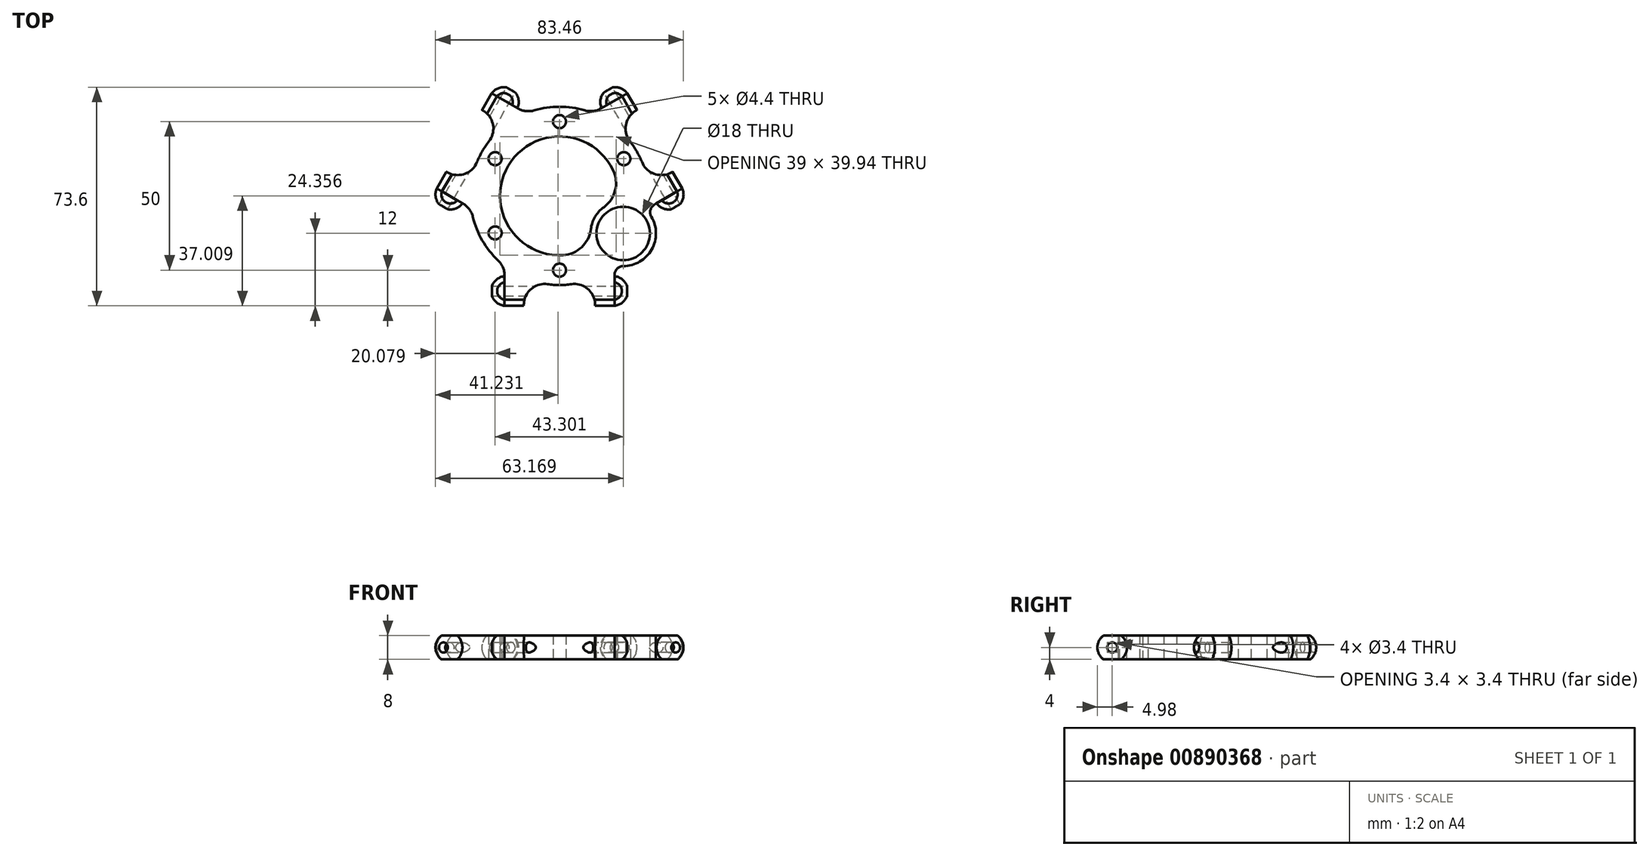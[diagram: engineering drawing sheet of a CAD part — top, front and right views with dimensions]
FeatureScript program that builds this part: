
annotation { "Feature Type Name" : "Feature", "Feature Type Description" : "" }
export const myFeature = defineFeature(function(context is Context, id is Id, definition is map)
    precondition{}
    {
        {
            var Q0;
            Q0=qCreatedBy(makeId("Top.planeOp"),FACE);
            var sketch = newSketch(context, id + "F0", { "sketchPlane" : qUnion([Q0])});
            skLineSegment(sketch, "E0", {"start": v(-16.34, 35.93) * mm, "end": v(-39.06, -3.47) * mm, "construction": true});
            skLineSegment(sketch, "E1", {"start": v(-40.4, -2.74) * mm, "end": v(-37.72, -4.2) * mm, "construction": true});
            skLineSegment(sketch, "E2", {"start": v(-17.63, 36.7) * mm, "end": v(-15.06, 35.15) * mm, "construction": true});
            skCircle(sketch, "E3", {"center": v(0, 0) * mm, "radius": 30 * mm});
            skCircle(sketch, "E4", {"center": v(0, 0) * mm, "radius": 20 * mm});
            skLineSegment(sketch, "E5", {"start": v(0, 0) * mm, "end": v(0, -43.55) * mm, "construction": true});
            skLineSegment(sketch, "E6", {"start": v(-25.45, -32) * mm, "end": v(35.74, -32) * mm, "construction": true});
            skLineSegment(sketch, "E7", {"start": v(-12, -37) * mm, "end": v(-12, -27.5) * mm});
            skLineSegment(sketch, "E8", {"start": v(-12, -37) * mm, "end": v(-18.5, -37) * mm});
            skLineSegment(sketch, "E9", {"start": v(-18.5, -37) * mm, "end": v(-18.5, -23.62) * mm});
            skLineSegment(sketch, "E10.MirrorCS", {"start": v(18.5, -37) * mm, "end": v(18.5, -23.62) * mm});
            skLineSegment(sketch, "E11.MirrorCS", {"start": v(12, -37) * mm, "end": v(12, -27.5) * mm});
            skLineSegment(sketch, "E12.MirrorCS", {"start": v(12, -37) * mm, "end": v(18.5, -37) * mm});
            skLineSegment(sketch, "E13.1.0", {"start": v(41.29, 2.48) * mm, "end": v(29.7, -4.21) * mm});
            skLineSegment(sketch, "E13.1.1", {"start": v(38.04, 8.1) * mm, "end": v(41.29, 2.48) * mm});
            skLineSegment(sketch, "E13.1.2", {"start": v(38.04, 8.1) * mm, "end": v(29.81, 3.36) * mm});
            skLineSegment(sketch, "E13.1.3", {"start": v(26.04, 28.9) * mm, "end": v(17.81, 24.14) * mm});
            skLineSegment(sketch, "E13.1.4", {"start": v(26.04, 28.9) * mm, "end": v(22.79, 34.52) * mm});
            skLineSegment(sketch, "E13.1.5", {"start": v(22.79, 34.52) * mm, "end": v(11.2, 27.83) * mm});
            skLineSegment(sketch, "E13.2.0", {"start": v(-22.79, 34.52) * mm, "end": v(-11.2, 27.83) * mm});
            skLineSegment(sketch, "E13.2.1", {"start": v(-26.04, 28.9) * mm, "end": v(-22.79, 34.52) * mm});
            skLineSegment(sketch, "E13.2.2", {"start": v(-26.04, 28.9) * mm, "end": v(-17.81, 24.14) * mm});
            skLineSegment(sketch, "E13.2.3", {"start": v(-38.04, 8.1) * mm, "end": v(-29.81, 3.36) * mm});
            skLineSegment(sketch, "E13.2.4", {"start": v(-38.04, 8.1) * mm, "end": v(-41.29, 2.48) * mm});
            skLineSegment(sketch, "E13.2.5", {"start": v(-41.29, 2.48) * mm, "end": v(-29.7, -4.21) * mm});
            skCircle(sketch, "E14", {"center": v(0, 25) * mm, "radius": 2.2 * mm});
            skCircle(sketch, "E15.1.0", {"center": v(-21.65, 12.5) * mm, "radius": 2.2 * mm});
            skCircle(sketch, "E15.2.0", {"center": v(-21.65, -12.5) * mm, "radius": 2.2 * mm});
            skCircle(sketch, "E15.3.0", {"center": v(0, -25) * mm, "radius": 2.2 * mm});
            skCircle(sketch, "E15.4.0", {"center": v(21.65, -12.5) * mm, "radius": 2.2 * mm});
            skCircle(sketch, "E15.5.0", {"center": v(21.65, 12.5) * mm, "radius": 2.2 * mm});
            skSolve(sketch);
        }
        {
            var Q0;
            Q0=qSketchRegion(id+"F0",true);
            extrude(context, id + "F1", {"entities" : qUnion([Q0]), "endBound" : BoundingType.SYMMETRIC, "depth" : 10 * mm, "offsetDistance" : 25 * mm});
        }
        {
            var Q0;
            Q0=qCreatedBy(makeId("Top.planeOp"),FACE);
            var sketch = newSketch(context, id + "F2", { "sketchPlane" : qUnion([Q0])});
            skArc(sketch, "E16", {"start": v(-23, -32.02) * mm, "mid": v(-21.7, -35.37) * mm, "end": v(-18.5, -37) * mm});
            skLineSegment(sketch, "E17", {"start": v(-18, -32.02) * mm, "end": v(-25.15, -32.02) * mm, "construction": true});
            skLineSegment(sketch, "E18", {"start": v(0, 0) * mm, "end": v(0, -44.37) * mm, "construction": true});
            skLineSegment(sketch, "E19", {"start": v(-39.92, 23.05) * mm, "end": v(0, 0) * mm, "construction": true});
            skLineSegment(sketch, "E20", {"start": v(0, 0) * mm, "end": v(41.5, 23.96) * mm, "construction": true});
            skLineSegment(sketch, "E21", {"start": v(-18.5, -37) * mm, "end": v(-18.5, -27.05) * mm});
            skLineSegment(sketch, "E22", {"start": v(-23, -32.02) * mm, "end": v(-18.5, -32.02) * mm});
            skArc(sketch, "E23.1.0", {"start": v(39.23, -3.9) * mm, "mid": v(41.49, -1.11) * mm, "end": v(41.29, 2.48) * mm});
            skLineSegment(sketch, "E23.1.1", {"start": v(39.23, -3.9) * mm, "end": v(36.98, -0.01) * mm});
            skArc(sketch, "E23.2.0", {"start": v(-16.23, 35.93) * mm, "mid": v(-19.78, 36.49) * mm, "end": v(-22.79, 34.52) * mm});
            skLineSegment(sketch, "E23.2.1", {"start": v(-16.23, 35.93) * mm, "end": v(-18.48, 32.03) * mm});
            skPoint(sketch, "E23.center", {"position": v(0, 0) * mm});
            skLineSegment(sketch, "E24.MirrorCS", {"start": v(23, -32.02) * mm, "end": v(18.5, -32.02) * mm});
            skLineSegment(sketch, "E25.MirrorCS", {"start": v(18, -32.02) * mm, "end": v(25.15, -32.02) * mm, "construction": true});
            skLineSegment(sketch, "E26.MirrorCS", {"start": v(18.5, -37) * mm, "end": v(18.5, -27.05) * mm});
            skArc(sketch, "E27.MirrorCS", {"start": v(23, -32.02) * mm, "mid": v(21.7, -35.37) * mm, "end": v(18.5, -37) * mm});
            skLineSegment(sketch, "E28", {"start": v(0, 0) * mm, "end": v(31.6, -18.24) * mm, "construction": true});
            skSolve(sketch);
        }
        {
            var Q0;
            Q0=qSketchRegion(id+"F2",true);
            var Q1;
            Q1=sQuery(id+"F2.wireOp",EDGE,"E17");
            revolve(context, id + "F3", {"surfaceOperationType" : NewSurfaceOperationType.NEW, "entities" : qUnion([Q0]), "axis" : qUnion([Q1]), "revolveType" : RevolveType.FULL});
        }
        {
            var Q0;
            Q0=qCreatedBy(makeId("Right.planeOp"),FACE);
            var sketch = newSketch(context, id + "F4", { "sketchPlane" : qUnion([Q0])});
            skLineSegment(sketch, "E29", {"start": v(0, 32.68) * mm, "end": v(0, -16.38) * mm, "construction": true});
            skSolve(sketch);
        }
        {
            var Q0;
            Q0=makeQuery(id+"F3.opRevolve","SWEPT_BODY",BODY,{"disambiguationData":[OSD([sQuery(id+"F2.wireOp",EDGE,"E16"),sQuery(id+"F2.wireOp",EDGE,"E21"),sQuery(id+"F2.wireOp",EDGE,"E22")])]});
            var Q1;
            Q1=makeQuery(id+"F3.opRevolve","SWEPT_BODY",BODY,{"disambiguationData":[OSD([sQuery(id+"F2.wireOp",EDGE,"E24.MirrorCS"),sQuery(id+"F2.wireOp",EDGE,"E26.MirrorCS"),sQuery(id+"F2.wireOp",EDGE,"E27.MirrorCS")])]});
            var Q2;
            Q2=sQuery(id+"F4.wireOp",EDGE,"E29");
            circularPattern(context, id + "F5", {"entities" : qUnion([Q0, Q1]), "axis" : qUnion([Q2]), "angle" : 360 * degree, "instanceCount" : 3, "equalSpace" : true});
        }
        {
            var Q0;
            Q0=makeQuery(id+"F1.opExtrude","CAP_EDGE",EDGE,{"disambiguationData":[OSD([sQuery(id+"F0.wireOp",EDGE,"E13.2.1")])],"isStart":false});
            var Q1;
            Q1=makeQuery(id+"F1.opExtrude","CAP_EDGE",EDGE,{"disambiguationData":[OSD([sQuery(id+"F0.wireOp",EDGE,"E13.2.4")])],"isStart":false});
            var Q2;
            Q2=makeQuery(id+"F1.opExtrude","CAP_EDGE",EDGE,{"disambiguationData":[OSD([sQuery(id+"F0.wireOp",EDGE,"E13.1.4")])],"isStart":false});
            var Q3;
            Q3=makeQuery(id+"F1.opExtrude","CAP_EDGE",EDGE,{"disambiguationData":[OSD([sQuery(id+"F0.wireOp",EDGE,"E13.1.1")])],"isStart":false});
            var Q4;
            Q4=makeQuery(id+"F1.opExtrude","CAP_EDGE",EDGE,{"disambiguationData":[OSD([sQuery(id+"F0.wireOp",EDGE,"E12.MirrorCS")])],"isStart":false});
            var Q5;
            Q5=makeQuery(id+"F1.opExtrude","CAP_EDGE",EDGE,{"disambiguationData":[OSD([sQuery(id+"F0.wireOp",EDGE,"E8")])],"isStart":false});
            var Q6;
            Q6=makeQuery(id+"F1.opExtrude","CAP_EDGE",EDGE,{"disambiguationData":[OSD([sQuery(id+"F0.wireOp",EDGE,"E8")])],"isStart":true});
            var Q7;
            Q7=makeQuery(id+"F1.opExtrude","CAP_EDGE",EDGE,{"disambiguationData":[OSD([sQuery(id+"F0.wireOp",EDGE,"E12.MirrorCS")])],"isStart":true});
            var Q8;
            Q8=makeQuery(id+"F1.opExtrude","CAP_EDGE",EDGE,{"disambiguationData":[OSD([sQuery(id+"F0.wireOp",EDGE,"E13.1.1")])],"isStart":true});
            var Q9;
            Q9=makeQuery(id+"F1.opExtrude","CAP_EDGE",EDGE,{"disambiguationData":[OSD([sQuery(id+"F0.wireOp",EDGE,"E13.1.4")])],"isStart":true});
            var Q10;
            Q10=makeQuery(id+"F1.opExtrude","CAP_EDGE",EDGE,{"disambiguationData":[OSD([sQuery(id+"F0.wireOp",EDGE,"E13.2.1")])],"isStart":true});
            var Q11;
            Q11=makeQuery(id+"F1.opExtrude","CAP_EDGE",EDGE,{"disambiguationData":[OSD([sQuery(id+"F0.wireOp",EDGE,"E13.2.4")])],"isStart":true});
            fillet(context, id + "F6", {"entities" : qUnion([Q0, Q1, Q2, Q3, Q4, Q5, Q6, Q7, Q8, Q9, Q10, Q11]), "radius" : 5 * mm, "tangentPropagation" : true, "allowEdgeOverflow" : false});
        }
        {
            var Q0;
            Q0=qCreatedBy(makeId("Top.planeOp"),FACE);
            var sketch = newSketch(context, id + "F7", { "sketchPlane" : qUnion([Q0])});
            skCircle(sketch, "E30", {"center": v(0, 0) * mm, "radius": 54.32 * mm});
            skSolve(sketch);
        }
        {
            var Q0;
            Q0=makeQuery(id+"F7.imprint","IMPRINT",FACE,{"disambiguationData":[TD([[makeQuery(id+"F7.imprint","IMPRINT",EDGE,{"derivedFrom":sQuery(id+"F7.wireOp",EDGE,"E30")}),1.0]])]});
            extrude(context, id + "F8", {"entities" : qUnion([Q0]), "operationType" : NewBodyOperationType.REMOVE, "depth" : 10 * mm, "offsetDistance" : 25 * mm, "hasSecondDirection" : true, "secondDirectionOppositeDirection" : false, "secondDirectionDepth" : 4 * mm});
        }
        {
            var Q0;
            Q0=makeQuery(id+"F7.imprint","IMPRINT",FACE,{"disambiguationData":[TD([[makeQuery(id+"F7.imprint","IMPRINT",EDGE,{"derivedFrom":sQuery(id+"F7.wireOp",EDGE,"E30")}),1.0]])]});
            extrude(context, id + "F9", {"entities" : qUnion([Q0]), "operationType" : NewBodyOperationType.REMOVE, "oppositeDirection" : true, "depth" : 20 * mm, "offsetDistance" : 25 * mm, "hasSecondDirection" : true, "secondDirectionOppositeDirection" : true, "secondDirectionDepth" : 4 * mm});
        }
        {
            var Q0;
            Q0=qCreatedBy(makeId("Right.planeOp"),FACE);
            var sketch = newSketch(context, id + "F10", { "sketchPlane" : qUnion([Q0])});
            skCircle(sketch, "E31", {"center": v(-32.02, 0) * mm, "radius": 1.7 * mm});
            skSolve(sketch);
        }
        {
            var Q0;
            Q0=qSketchRegion(id+"F10",true);
            extrude(context, id + "F11", {"entities" : qUnion([Q0]), "operationType" : NewBodyOperationType.REMOVE, "endBound" : BoundingType.SYMMETRIC, "oppositeDirection" : true, "depth" : 80 * mm, "offsetDistance" : 25 * mm});
        }
        {
            var Q0;
            Q0=sQuery(id+"F2.wireOp",EDGE,"E19");
            cPlane(context, id + "F12", {"entities" : qUnion([Q0]), "cplaneType" : CPlaneType.LINE_ANGLE, "offset" : 25 * mm, "angle" : 0 * degree, "width" : 150 * mm, "height" : 150 * mm});
        }
        {
            var Q0;
            Q0=qCreatedBy(id+"F12.planeOp",FACE);
            var sketch = newSketch(context, id + "F13", { "sketchPlane" : qUnion([Q0])});
            skCircle(sketch, "E32", {"center": v(32.02, 0) * mm, "radius": 1.7 * mm});
            skSolve(sketch);
        }
        {
            var Q0;
            Q0=qSketchRegion(id+"F13",true);
            extrude(context, id + "F14", {"entities" : qUnion([Q0]), "operationType" : NewBodyOperationType.REMOVE, "endBound" : BoundingType.SYMMETRIC, "oppositeDirection" : true, "depth" : 80 * mm, "offsetDistance" : 25 * mm});
        }
        {
            var Q0;
            Q0=sQuery(id+"F2.wireOp",EDGE,"E20");
            cPlane(context, id + "F15", {"entities" : qUnion([Q0]), "cplaneType" : CPlaneType.LINE_ANGLE, "offset" : 25 * mm, "angle" : 0 * degree, "width" : 150 * mm, "height" : 150 * mm});
        }
        {
            var Q0;
            Q0=qCreatedBy(id+"F15.planeOp",FACE);
            var sketch = newSketch(context, id + "F16", { "sketchPlane" : qUnion([Q0])});
            skCircle(sketch, "E33", {"center": v(-32.02, 0) * mm, "radius": 1.7 * mm});
            skSolve(sketch);
        }
        {
            var Q0;
            Q0=qSketchRegion(id+"F16",true);
            extrude(context, id + "F17", {"entities" : qUnion([Q0]), "operationType" : NewBodyOperationType.REMOVE, "endBound" : BoundingType.SYMMETRIC, "oppositeDirection" : true, "depth" : 80 * mm, "offsetDistance" : 25 * mm});
        }
        {
            var Q0;
            Q0=makeQuery(id+"F1.opExtrude","SWEPT_EDGE",EDGE,{"disambiguationData":[OSD([sQuery(id+"F0.wireOp",EDGE,"E3"),sQuery(id+"F0.wireOp",EDGE,"E13.2.0")])]});
            var Q1;
            Q1=makeQuery(id+"F1.opExtrude","SWEPT_EDGE",EDGE,{"disambiguationData":[OSD([sQuery(id+"F0.wireOp",EDGE,"E3"),sQuery(id+"F0.wireOp",EDGE,"E13.1.5")])]});
            var Q2;
            Q2=makeQuery(id+"F1.opExtrude","SWEPT_EDGE",EDGE,{"disambiguationData":[OSD([sQuery(id+"F0.wireOp",EDGE,"E3"),sQuery(id+"F0.wireOp",EDGE,"E13.1.0")])]});
            var Q3;
            Q3=makeQuery(id+"F1.opExtrude","SWEPT_EDGE",EDGE,{"disambiguationData":[OSD([sQuery(id+"F0.wireOp",EDGE,"E3"),sQuery(id+"F0.wireOp",EDGE,"E10.MirrorCS")])]});
            var Q4;
            Q4=makeQuery(id+"F1.opExtrude","SWEPT_EDGE",EDGE,{"disambiguationData":[OSD([sQuery(id+"F0.wireOp",EDGE,"E3"),sQuery(id+"F0.wireOp",EDGE,"E13.2.5")])]});
            var Q5;
            Q5=makeQuery(id+"F1.opExtrude","SWEPT_EDGE",EDGE,{"disambiguationData":[OSD([sQuery(id+"F0.wireOp",EDGE,"E3"),sQuery(id+"F0.wireOp",EDGE,"E9")])]});
            fillet(context, id + "F18", {"entities" : qUnion([Q0, Q1, Q2, Q3, Q4, Q5]), "radius" : 7 * mm, "tangentPropagation" : true, "allowEdgeOverflow" : false});
        }
        {
            var Q0;
            Q0=qCreatedBy(makeId("Top.planeOp"),FACE);
            cPlane(context, id + "F19", {"entities" : qUnion([Q0]), "cplaneType" : CPlaneType.OFFSET, "offset" : 25 * mm, "width" : 150 * mm, "height" : 150 * mm});
        }
        {
            var Q0;
            Q0=qCreatedBy(makeId("Top.planeOp"),FACE);
            var sketch = newSketch(context, id + "F20", { "sketchPlane" : qUnion([Q0])});
            skCircle(sketch, "E34", {"center": v(21.44, -12.64) * mm, "radius": 11 * mm});
            skCircle(sketch, "E35", {"center": v(21.44, -12.64) * mm, "radius": 9 * mm});
            skSolve(sketch);
        }
        {
            var Q0;
            Q0=makeQuery(id+"F20.imprint","IMPRINT",FACE,{"disambiguationData":[TD([[makeQuery(id+"F20.imprint","IMPRINT",EDGE,{"derivedFrom":sQuery(id+"F20.wireOp",EDGE,"E35")}),1.0]])]});
            extrude(context, id + "F21", {"entities" : qUnion([Q0]), "operationType" : NewBodyOperationType.REMOVE, "endBound" : BoundingType.SYMMETRIC, "oppositeDirection" : true, "depth" : 25 * mm, "offsetDistance" : 25 * mm});
        }
        {
            var Q0;
            Q0=makeQuery(id+"F20.imprint","IMPRINT",FACE,{"disambiguationData":[TD([[makeQuery(id+"F20.imprint","IMPRINT",EDGE,{"derivedFrom":sQuery(id+"F20.wireOp",EDGE,"E34")}),1.0]])]});
            extrude(context, id + "F22", {"entities" : qUnion([Q0]), "operationType" : NewBodyOperationType.ADD, "endBound" : BoundingType.SYMMETRIC, "depth" : 8 * mm, "offsetDistance" : 25 * mm});
        }
        {
            var Q0;
            Q0=makeQuery(id+"F22.boolean.opBoolean","INTERSECT",EDGE,{"derivedFrom":[makeQuery(id+"F18.opFillet","BLEND_FACE",FACE,{"disambiguationData":[OSD([sQuery(id+"F0.wireOp",EDGE,"E3"),sQuery(id+"F0.wireOp",EDGE,"E13.1.0")])]}),makeQuery(id+"F22.opExtrude","SWEPT_FACE",FACE,{"disambiguationData":[OSD([sQuery(id+"F20.wireOp",EDGE,"E34")])]})]});
            var Q1;
            Q1=makeQuery(id+"F22.boolean.opBoolean","INTERSECT",EDGE,{"derivedFrom":[makeQuery(id+"F18.opFillet","BLEND_FACE",FACE,{"disambiguationData":[OSD([sQuery(id+"F0.wireOp",EDGE,"E3"),sQuery(id+"F0.wireOp",EDGE,"E10.MirrorCS")])]}),makeQuery(id+"F22.opExtrude","SWEPT_FACE",FACE,{"disambiguationData":[OSD([sQuery(id+"F20.wireOp",EDGE,"E34")])]})]});
            fillet(context, id + "F23", {"entities" : qUnion([Q0, Q1]), "radius" : 3 * mm, "tangentPropagation" : true, "allowEdgeOverflow" : false});
        }
        {
            var Q0;
            Q0=makeQuery(id+"F22.boolean.opBoolean","INTERSECT",EDGE,{"disambiguationData":[OD(0.0)],"derivedFrom":[makeQuery(id+"F1.opExtrude","SWEPT_FACE",FACE,{"disambiguationData":[OSD([sQuery(id+"F0.wireOp",EDGE,"E4")])]}),makeQuery(id+"F22.opExtrude","SWEPT_FACE",FACE,{"disambiguationData":[OSD([sQuery(id+"F20.wireOp",EDGE,"E34")])]})]});
            var Q1;
            Q1=makeQuery(id+"F22.boolean.opBoolean","INTERSECT",EDGE,{"disambiguationData":[OD(1.0)],"derivedFrom":[makeQuery(id+"F1.opExtrude","SWEPT_FACE",FACE,{"disambiguationData":[OSD([sQuery(id+"F0.wireOp",EDGE,"E4")])]}),makeQuery(id+"F22.opExtrude","SWEPT_FACE",FACE,{"disambiguationData":[OSD([sQuery(id+"F20.wireOp",EDGE,"E34")])]})]});
            fillet(context, id + "F24", {"entities" : qUnion([Q0, Q1]), "radius" : 10 * mm, "tangentPropagation" : true, "allowEdgeOverflow" : false});
        }
    });
